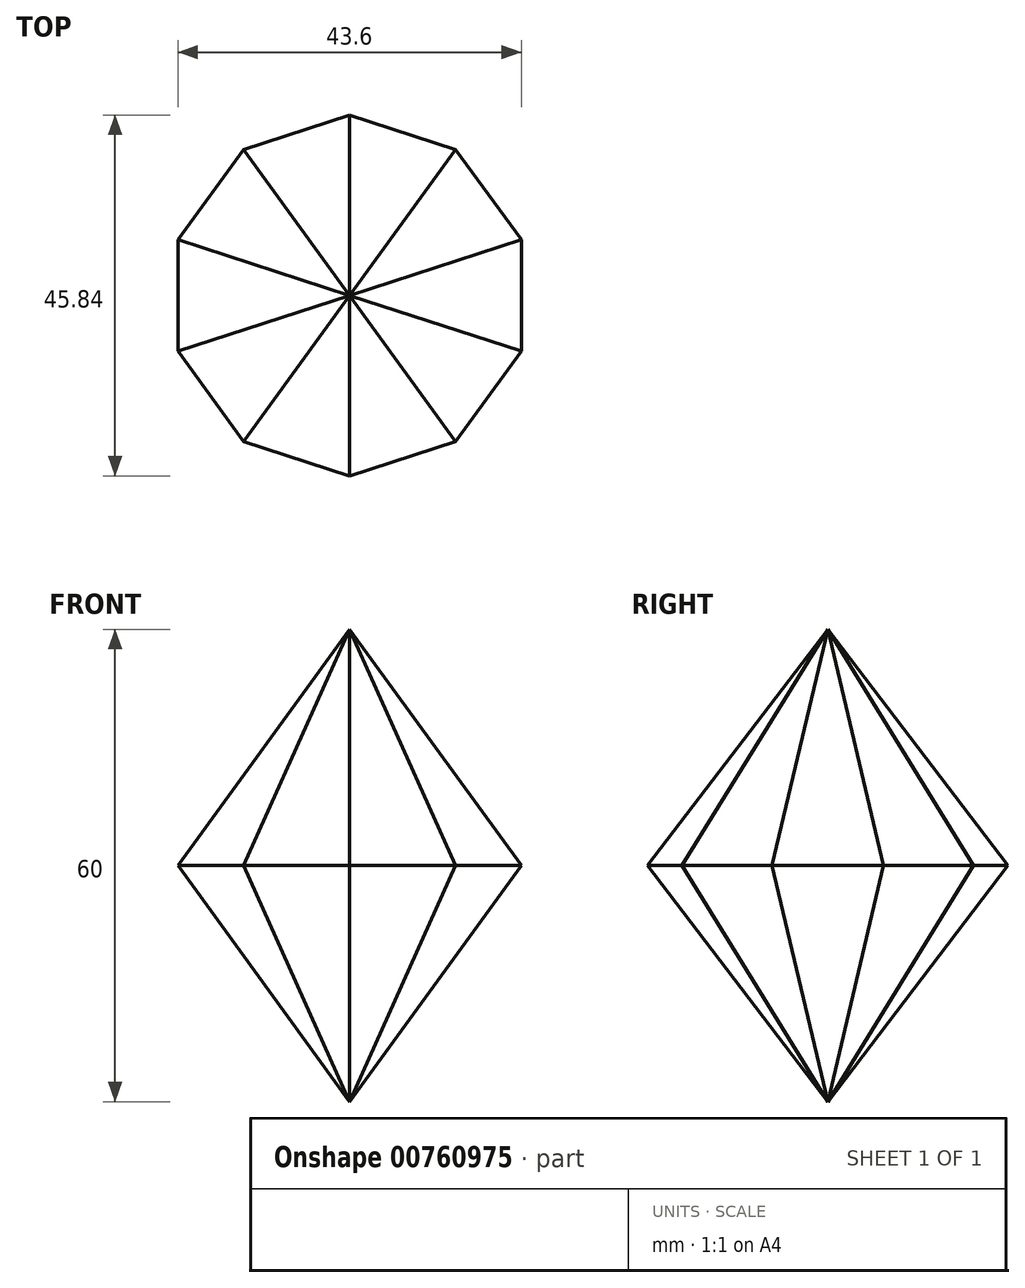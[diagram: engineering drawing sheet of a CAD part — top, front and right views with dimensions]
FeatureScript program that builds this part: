
annotation { "Feature Type Name" : "Feature", "Feature Type Description" : "" }
export const myFeature = defineFeature(function(context is Context, id is Id, definition is map)
    precondition{}
    {
        {
            var Q0;
            Q0=qCreatedBy(makeId("Top.planeOp"),FACE);
            var sketch = newSketch(context, id + "F0", { "sketchPlane" : qUnion([Q0])});
            skCircle(sketch, "E0.cCircle", {"center": v(0, 0) * mm, "radius": 30 * mm, "construction": true});
            skLineSegment(sketch, "E0.0", {"start": v(-21.8, 30) * mm, "end": v(21.8, 30) * mm});
            skLineSegment(sketch, "E0.1", {"start": v(21.8, 30) * mm, "end": v(35.27, -11.46) * mm});
            skLineSegment(sketch, "E0.2", {"start": v(35.27, -11.46) * mm, "end": v(0, -37.08) * mm});
            skLineSegment(sketch, "E0.3", {"start": v(0, -37.08) * mm, "end": v(-35.27, -11.46) * mm});
            skLineSegment(sketch, "E0.4", {"start": v(-35.27, -11.46) * mm, "end": v(-21.8, 30) * mm});
            skPoint(sketch, "E0.0.midPoint", {"position": v(0, 30) * mm});
            skSolve(sketch);
        }
        {
            var Q0;
            Q0=qSketchRegion(id+"F0",true);
            extrude(context, id + "F1", {"entities" : qUnion([Q0]), "endBound" : BoundingType.SYMMETRIC, "depth" : 60 * mm});
        }
        {
            var Q0;
            Q0=makeQuery(id+"F1.opExtrude","SWEPT_FACE",FACE,{"disambiguationData":[OSD([sQuery(id+"F0.wireOp",EDGE,"E0.3")])]});
            var sketch = newSketch(context, id + "F2", { "sketchPlane" : qUnion([Q0])});
            skLineSegment(sketch, "E1", {"start": v(0, 30) * mm, "end": v(-21.8, 0) * mm});
            skLineSegment(sketch, "E2", {"start": v(-21.8, 0) * mm, "end": v(0, -30) * mm});
            skLineSegment(sketch, "E3", {"start": v(0, -30) * mm, "end": v(21.8, 0) * mm});
            skLineSegment(sketch, "E4", {"start": v(21.8, 0) * mm, "end": v(0, 30) * mm});
            skSolve(sketch);
        }
        {
            var Q0;
            Q0=makeQuery(id+"F1.opExtrude","SWEPT_FACE",FACE,{"disambiguationData":[OSD([sQuery(id+"F0.wireOp",EDGE,"E0.2")])]});
            var sketch = newSketch(context, id + "F3", { "sketchPlane" : qUnion([Q0])});
            skLineSegment(sketch, "E5", {"start": v(-21.8, 0) * mm, "end": v(0, 30) * mm});
            skLineSegment(sketch, "E6", {"start": v(0, 30) * mm, "end": v(21.8, 0) * mm});
            skLineSegment(sketch, "E7", {"start": v(21.8, 0) * mm, "end": v(0, -30) * mm});
            skLineSegment(sketch, "E8", {"start": v(0, -30) * mm, "end": v(-21.8, 0) * mm});
            skSolve(sketch);
        }
        {
            var Q0;
            Q0=makeQuery(id+"F1.opExtrude","SWEPT_FACE",FACE,{"disambiguationData":[OSD([sQuery(id+"F0.wireOp",EDGE,"E0.4")])]});
            var sketch = newSketch(context, id + "F4", { "sketchPlane" : qUnion([Q0])});
            skLineSegment(sketch, "E9", {"start": v(21.8, 0) * mm, "end": v(0, 30) * mm});
            skLineSegment(sketch, "E10", {"start": v(0, 30) * mm, "end": v(-21.8, 0) * mm});
            skLineSegment(sketch, "E11", {"start": v(-21.8, 0) * mm, "end": v(0, -30) * mm});
            skLineSegment(sketch, "E12", {"start": v(0, -30) * mm, "end": v(21.8, 0) * mm});
            skSolve(sketch);
        }
        {
            var Q0;
            Q0=makeQuery(id+"F1.opExtrude","SWEPT_FACE",FACE,{"disambiguationData":[OSD([sQuery(id+"F0.wireOp",EDGE,"E0.1")])]});
            var sketch = newSketch(context, id + "F5", { "sketchPlane" : qUnion([Q0])});
            skLineSegment(sketch, "E13", {"start": v(21.8, 0) * mm, "end": v(0, 30) * mm});
            skLineSegment(sketch, "E14", {"start": v(0, 30) * mm, "end": v(-21.8, 0) * mm});
            skLineSegment(sketch, "E15", {"start": v(-21.8, 0) * mm, "end": v(0, -30) * mm});
            skLineSegment(sketch, "E16", {"start": v(0, -30) * mm, "end": v(21.8, 0) * mm});
            skSolve(sketch);
        }
        {
            var Q0;
            Q0=makeQuery(id+"F1.opExtrude","SWEPT_FACE",FACE,{"disambiguationData":[OSD([sQuery(id+"F0.wireOp",EDGE,"E0.0")])]});
            var sketch = newSketch(context, id + "F6", { "sketchPlane" : qUnion([Q0])});
            skLineSegment(sketch, "E17", {"start": v(21.8, 0) * mm, "end": v(0, 30) * mm});
            skLineSegment(sketch, "E18", {"start": v(0, 30) * mm, "end": v(-21.8, 0) * mm});
            skLineSegment(sketch, "E19", {"start": v(-21.8, 0) * mm, "end": v(0, -30) * mm});
            skLineSegment(sketch, "E20", {"start": v(0, -30) * mm, "end": v(21.8, 0) * mm});
            skSolve(sketch);
        }
        {
            var Q0;
            Q0=qSketchRegion(id+"F2",true);
            extrude(context, id + "F7", {"entities" : qUnion([Q0]), "operationType" : NewBodyOperationType.INTERSECT, "endBound" : BoundingType.THROUGH_ALL, "oppositeDirection" : true, "depth" : 25 * mm});
        }
        {
            var Q0;
            Q0=qSketchRegion(id+"F3",true);
            extrude(context, id + "F8", {"entities" : qUnion([Q0]), "operationType" : NewBodyOperationType.INTERSECT, "endBound" : BoundingType.THROUGH_ALL, "oppositeDirection" : true, "depth" : 25 * mm});
        }
        {
            var Q0;
            Q0=qSketchRegion(id+"F4",true);
            extrude(context, id + "F9", {"entities" : qUnion([Q0]), "operationType" : NewBodyOperationType.INTERSECT, "endBound" : BoundingType.THROUGH_ALL, "oppositeDirection" : true, "depth" : 25 * mm});
        }
        {
            var Q0;
            Q0=qSketchRegion(id+"F5",true);
            extrude(context, id + "F10", {"entities" : qUnion([Q0]), "operationType" : NewBodyOperationType.INTERSECT, "endBound" : BoundingType.THROUGH_ALL, "oppositeDirection" : true, "depth" : 25 * mm});
        }
        {
            var Q0;
            Q0=qSketchRegion(id+"F6",true);
            extrude(context, id + "F11", {"entities" : qUnion([Q0]), "operationType" : NewBodyOperationType.INTERSECT, "endBound" : BoundingType.THROUGH_ALL, "oppositeDirection" : true, "depth" : 25 * mm});
        }
    });
